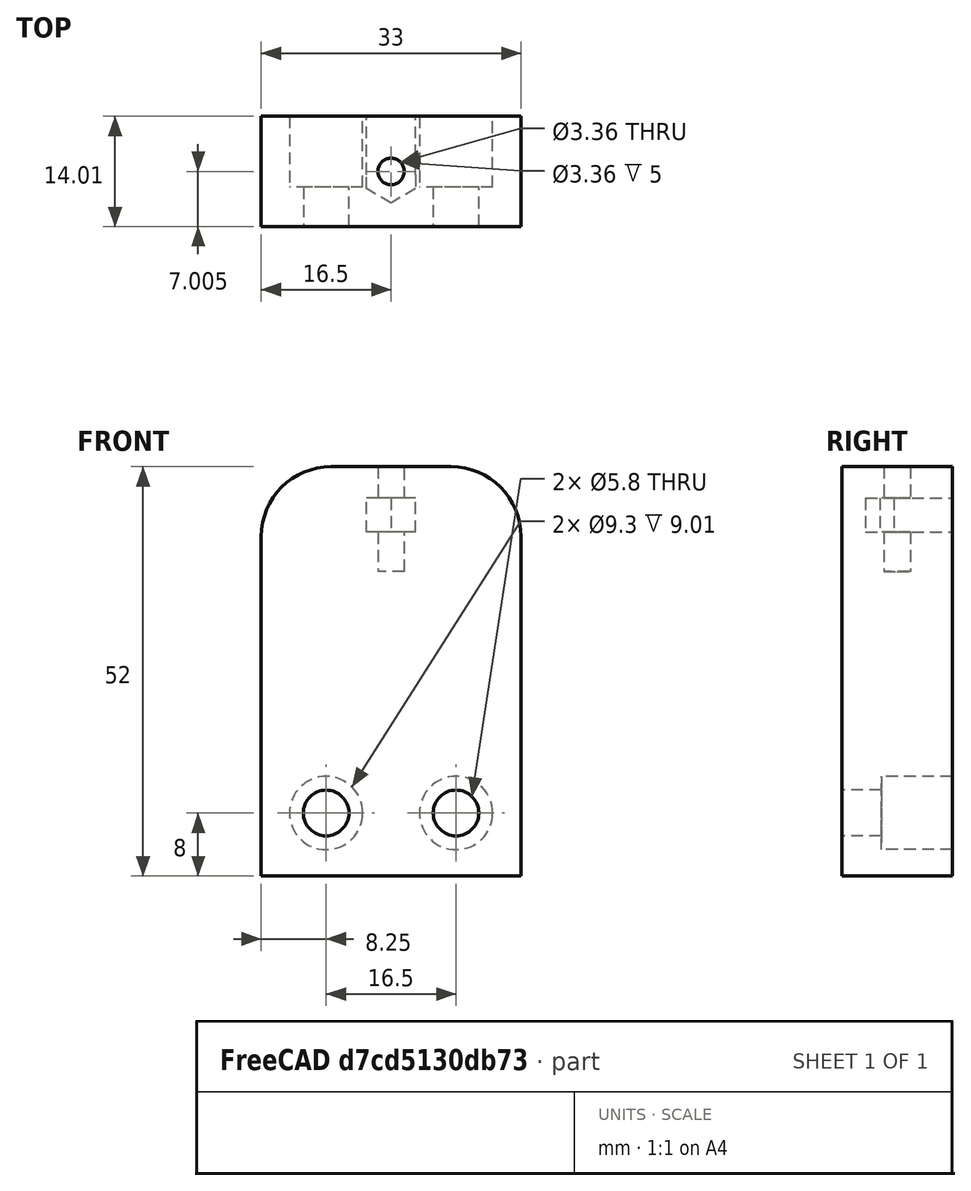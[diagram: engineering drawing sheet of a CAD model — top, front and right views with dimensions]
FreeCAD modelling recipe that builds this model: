
FCSTD DOCUMENT  (FreeCAD 0.16R6706 (Git))
Label: idler_pulley_holder_34_above_h
License: All rights reserved
LicenseURL: http://en.wikipedia.org/wiki/All_rights_reserved
objects: Part::Feature×1, Part::Fillet×1, Part::Prism×1, Part::Box×1, Part::Fuse×1, Part::Cut×1
note: 6 computed .brp shape members not serialized (recipe doc carries the construction recipe); baked Part::Feature solids carry a one-line shape summary decoded from their .brp

FEATURE [Part::Feature] idlepulleyhold_aux
  shape: bbox 33 x 14.01 x 52 mm, 14 faces (baked)
FEATURE [Part::Fillet] idlepulleyhold_chmf
  Base = -> idlepulleyhold_aux
  Edges = 2 edges r=8.895: [Edge9,Edge12]
FEATURE [Part::Prism] idlepulleyhold_nuthole_nut
  Circumradius = 3.605
  Height = 4.32
  Placement = pos=(0,0,0) rot=(-0.57735,0.57735,0.57735;2.0944rad)
  Polygon = 6
FEATURE [Part::Box] idlepulleyhold_nuthole_hole
  Height = 8.405
  Length = 6.24408
  Placement = pos=(-3.12204,0,0) rot=(0,0,1;0rad)
  Width = 4.32
FEATURE [Part::Fuse] idlepulleyhold_nuthole
  Base = -> idlepulleyhold_nuthole_nut
  Placement = pos=(0,6.605,30) rot=(-1,0,0;1.5708rad)
  Tool = -> idlepulleyhold_nuthole_hole
FEATURE [Part::Cut] idlepulleyhold
  Base = -> idlepulleyhold_chmf
  Tool = -> idlepulleyhold_nuthole
